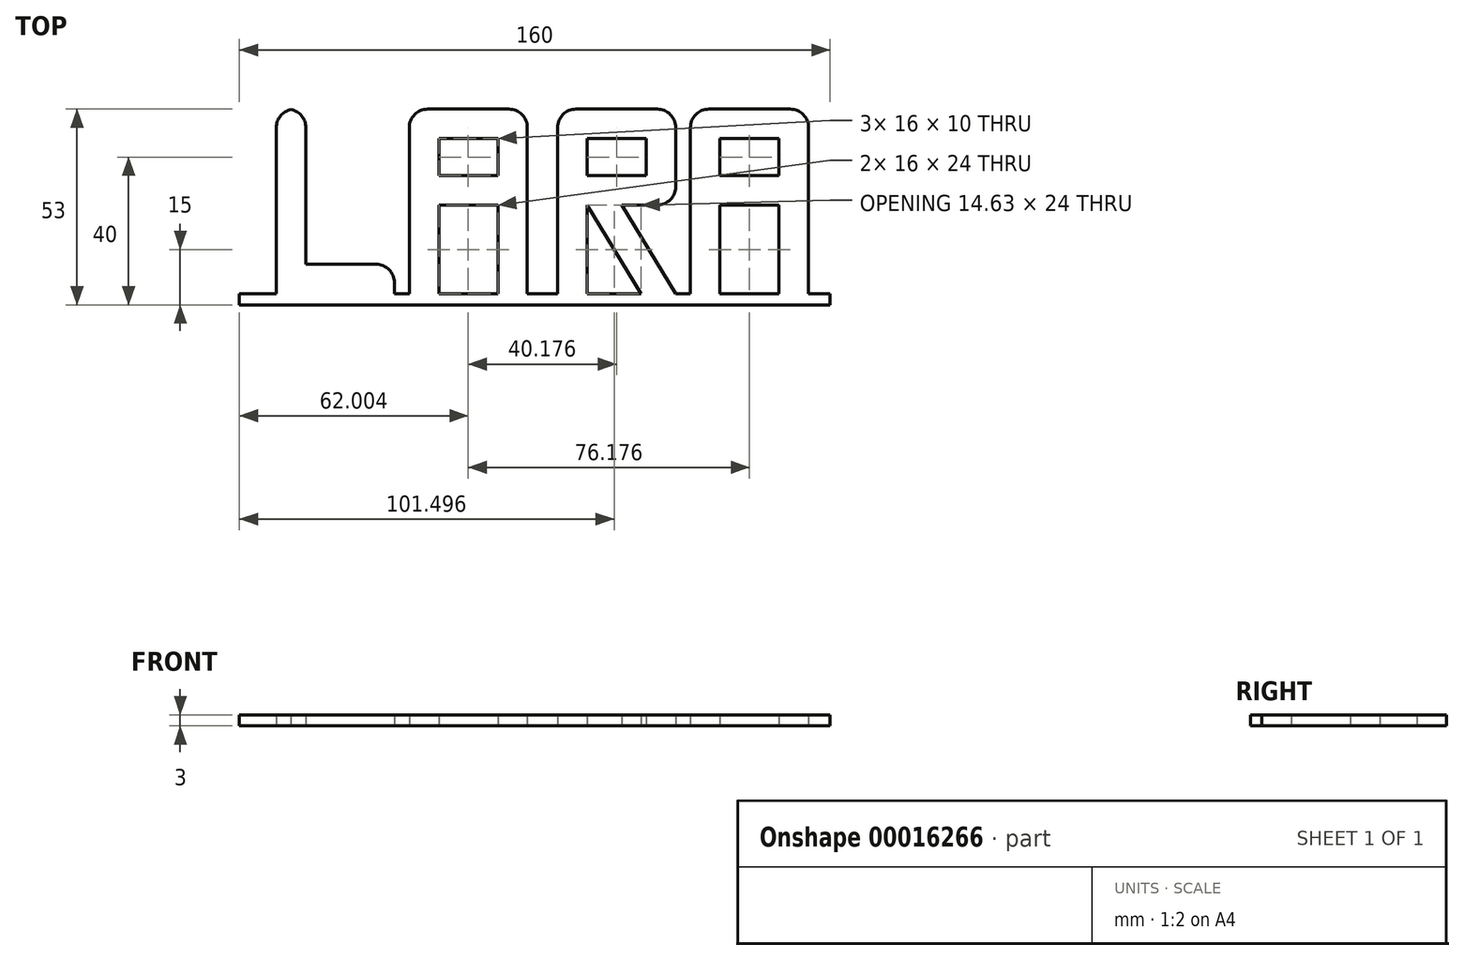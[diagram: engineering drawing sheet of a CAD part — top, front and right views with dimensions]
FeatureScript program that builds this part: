
annotation { "Feature Type Name" : "Feature", "Feature Type Description" : "" }
export const myFeature = defineFeature(function(context is Context, id is Id, definition is map)
    precondition{}
    {
        {
            var Q0;
            Q0=qCreatedBy(makeId("Top.planeOp"),FACE);
            var sketch = newSketch(context, id + "F0", { "sketchPlane" : qUnion([Q0])});
            skLineSegment(sketch, "E0.rect.bottom", {"start": v(71.24, 0) * mm, "end": v(-88.76, 0) * mm});
            skLineSegment(sketch, "E0.rect.top", {"start": v(71.24, 3) * mm, "end": v(-88.76, 3) * mm});
            skLineSegment(sketch, "E0.rect.left", {"start": v(71.24, 0) * mm, "end": v(71.24, 3) * mm});
            skLineSegment(sketch, "E0.rect.right", {"start": v(-88.76, 0) * mm, "end": v(-88.76, 3) * mm});
            skPoint(sketch, "E0.rect.middle", {"position": v(-8.76, 1.5) * mm});
            skSolve(sketch);
        }
        {
            var Q0;
            Q0 = qSketchRegion(id + "F0", true);
            extrude(context, id + "F1", {"entities" : qUnion([Q0]), "depth" : 3 * mm});
        }
        {
            var Q0;
            Q0=qCreatedBy(makeId("Top.planeOp"),FACE);
            var sketch = newSketch(context, id + "F2", { "sketchPlane" : qUnion([Q0])});
            skLineSegment(sketch, "E1.bottom", {"start": v(-78.76, 53) * mm, "end": v(-70.76, 53) * mm});
            skLineSegment(sketch, "E1.top", {"start": v(-78.76, 3) * mm, "end": v(-46.76, 3) * mm});
            skLineSegment(sketch, "E1.left", {"start": v(-78.76, 53) * mm, "end": v(-78.76, 3) * mm});
            skLineSegment(sketch, "E1.right", {"start": v(-46.76, 11) * mm, "end": v(-46.76, 3) * mm});
            skLineSegment(sketch, "E2.top", {"start": v(-46.76, 11) * mm, "end": v(-70.76, 11) * mm});
            skLineSegment(sketch, "E2.right", {"start": v(-70.76, 53) * mm, "end": v(-70.76, 11) * mm});
            skSolve(sketch);
        }
        {
            var Q0;
            Q0=makeQuery(id+"F2.imprint","IMPRINT",FACE,{"disambiguationData":[TD([[makeQuery(id+"F2.imprint","IMPRINT",EDGE,{"derivedFrom":sQuery(id+"F2.wireOp",EDGE,"E1.bottom")}),-1.0]])]});
            extrude(context, id + "F3", {"entities" : qUnion([Q0]), "operationType" : NewBodyOperationType.ADD, "depth" : 3 * mm});
        }
        {
            var Q0;
            Q0=qCreatedBy(makeId("Top.planeOp"),FACE);
            var sketch = newSketch(context, id + "F4", { "sketchPlane" : qUnion([Q0])});
            skLineSegment(sketch, "E3.bottom", {"start": v(-42.76, 3) * mm, "end": v(-10.76, 3) * mm});
            skLineSegment(sketch, "E3.top", {"start": v(-42.76, 53) * mm, "end": v(-10.76, 53) * mm});
            skLineSegment(sketch, "E3.left", {"start": v(-42.76, 3) * mm, "end": v(-42.76, 53) * mm});
            skLineSegment(sketch, "E3.right", {"start": v(-10.76, 3) * mm, "end": v(-10.76, 53) * mm});
            skLineSegment(sketch, "E4.bottom", {"start": v(-34.76, 3) * mm, "end": v(-18.76, 3) * mm});
            skLineSegment(sketch, "E4.top", {"start": v(-34.76, 27) * mm, "end": v(-18.76, 27) * mm});
            skLineSegment(sketch, "E4.left", {"start": v(-34.76, 3) * mm, "end": v(-34.76, 27) * mm});
            skLineSegment(sketch, "E4.right", {"start": v(-18.76, 3) * mm, "end": v(-18.76, 27) * mm});
            skLineSegment(sketch, "E5.bottom", {"start": v(-34.76, 45) * mm, "end": v(-18.76, 45) * mm});
            skLineSegment(sketch, "E5.top", {"start": v(-34.76, 35) * mm, "end": v(-18.76, 35) * mm});
            skLineSegment(sketch, "E5.left", {"start": v(-34.76, 45) * mm, "end": v(-34.76, 35) * mm});
            skLineSegment(sketch, "E5.right", {"start": v(-18.76, 45) * mm, "end": v(-18.76, 35) * mm});
            skSolve(sketch);
        }
        {
            var Q0;
            Q0=makeQuery(id+"F4.imprint","IMPRINT",FACE,{"disambiguationData":[TD([[makeQuery(id+"F4.imprint","IMPRINT",EDGE,{"derivedFrom":sQuery(id+"F4.wireOp",EDGE,"E3.top")}),-1.0]])]});
            extrude(context, id + "F5", {"entities" : qUnion([Q0]), "operationType" : NewBodyOperationType.ADD, "depth" : 3 * mm});
        }
        {
            var Q0;
            Q0=qCreatedBy(makeId("Top.planeOp"),FACE);
            var sketch = newSketch(context, id + "F6", { "sketchPlane" : qUnion([Q0])});
            skLineSegment(sketch, "E6.bottom", {"start": v(-2.58, 53) * mm, "end": v(29.42, 53) * mm});
            skLineSegment(sketch, "E6.top", {"start": v(-2.58, 3) * mm, "end": v(29.42, 3) * mm});
            skLineSegment(sketch, "E6.left", {"start": v(-2.58, 53) * mm, "end": v(-2.58, 3) * mm});
            skLineSegment(sketch, "E6.right", {"start": v(29.42, 53) * mm, "end": v(29.42, 3) * mm});
            skLineSegment(sketch, "E7.bottom", {"start": v(5.42, 45) * mm, "end": v(21.42, 45) * mm});
            skLineSegment(sketch, "E7.top", {"start": v(5.42, 35) * mm, "end": v(21.42, 35) * mm});
            skLineSegment(sketch, "E7.left", {"start": v(5.42, 45) * mm, "end": v(5.42, 35) * mm});
            skLineSegment(sketch, "E7.right", {"start": v(21.42, 45) * mm, "end": v(21.42, 35) * mm});
            skLineSegment(sketch, "E8", {"start": v(5.42, 27) * mm, "end": v(5.42, 3) * mm});
            skLineSegment(sketch, "E9", {"start": v(29.42, 3) * mm, "end": v(14.8, 27) * mm});
            skLineSegment(sketch, "E10", {"start": v(14.8, 27) * mm, "end": v(29.42, 27) * mm});
            skLineSegment(sketch, "E11", {"start": v(5.42, 27) * mm, "end": v(20.05, 3) * mm});
            skSolve(sketch);
        }
        {
            var Q0;
            {var subQ5=sQuery(id+"F6.wireOp",EDGE,"E6.bottom");Q0=makeQuery(id+"F6.imprint","IMPRINT",FACE,{"disambiguationData":[TD([[makeQuery(id+"F6.imprint","IMPRINT",EDGE,{"derivedFrom":subQ5}),-1.0]])]});}
            extrude(context, id + "F7", {"entities" : qUnion([Q0]), "operationType" : NewBodyOperationType.ADD, "depth" : 3 * mm});
        }
        {
            var Q0;
            Q0=makeQuery(id+"F3.opExtrude","SWEPT_EDGE",EDGE,{"disambiguationData":[OSD([sQuery(id+"F2.wireOp",EDGE,"E1.bottom"),sQuery(id+"F2.wireOp",EDGE,"E1.left")])]});
            var Q1;
            Q1=makeQuery(id+"F3.opExtrude","SWEPT_EDGE",EDGE,{"disambiguationData":[OSD([sQuery(id+"F2.wireOp",EDGE,"E1.bottom"),sQuery(id+"F2.wireOp",EDGE,"E2.right")])]});
            var Q2;
            Q2=makeQuery(id+"F5.opExtrude","SWEPT_EDGE",EDGE,{"disambiguationData":[OSD([sQuery(id+"F4.wireOp",EDGE,"E3.top"),sQuery(id+"F4.wireOp",EDGE,"E3.left")])]});
            var Q3;
            Q3=makeQuery(id+"F5.opExtrude","SWEPT_EDGE",EDGE,{"disambiguationData":[OSD([sQuery(id+"F4.wireOp",EDGE,"E3.top"),sQuery(id+"F4.wireOp",EDGE,"E3.right")])]});
            var Q4;
            Q4=makeQuery(id+"F7.opExtrude","SWEPT_EDGE",EDGE,{"disambiguationData":[OSD([sQuery(id+"F6.wireOp",EDGE,"E6.bottom"),sQuery(id+"F6.wireOp",EDGE,"E6.left")])]});
            var Q5;
            Q5=makeQuery(id+"F7.opExtrude","SWEPT_EDGE",EDGE,{"disambiguationData":[OSD([sQuery(id+"F6.wireOp",EDGE,"E6.bottom"),sQuery(id+"F6.wireOp",EDGE,"E6.right")])]});
            var Q6;
            Q6=makeQuery(id+"F3.opExtrude","SWEPT_EDGE",EDGE,{"disambiguationData":[OSD([sQuery(id+"F2.wireOp",EDGE,"E1.right"),sQuery(id+"F2.wireOp",EDGE,"E2.top")])]});
            var Q7;
            Q7=makeQuery(id+"F7.opExtrude","SWEPT_EDGE",EDGE,{"disambiguationData":[OSD([sQuery(id+"F6.wireOp",EDGE,"E6.right"),sQuery(id+"F6.wireOp",EDGE,"E10")])]});
            fillet(context, id + "F8", {"entities" : qUnion([Q0, Q1, Q2, Q3, Q4, Q5, Q6, Q7]), "radius" : 5 * mm, "tangentPropagation" : true, "allowEdgeOverflow" : false});
        }
        {
            var Q0;
            Q0=qCreatedBy(makeId("Top.planeOp"),FACE);
            var sketch = newSketch(context, id + "F9", { "sketchPlane" : qUnion([Q0])});
            skLineSegment(sketch, "E12.bottom", {"start": v(33.42, 3) * mm, "end": v(65.42, 3) * mm});
            skLineSegment(sketch, "E12.top", {"start": v(33.42, 53) * mm, "end": v(65.42, 53) * mm});
            skLineSegment(sketch, "E12.left", {"start": v(33.42, 3) * mm, "end": v(33.42, 53) * mm});
            skLineSegment(sketch, "E12.right", {"start": v(65.42, 3) * mm, "end": v(65.42, 53) * mm});
            skLineSegment(sketch, "E13.bottom", {"start": v(41.42, 45) * mm, "end": v(57.42, 45) * mm});
            skLineSegment(sketch, "E13.top", {"start": v(41.42, 35) * mm, "end": v(57.42, 35) * mm});
            skLineSegment(sketch, "E13.left", {"start": v(41.42, 45) * mm, "end": v(41.42, 35) * mm});
            skLineSegment(sketch, "E13.right", {"start": v(57.42, 45) * mm, "end": v(57.42, 35) * mm});
            skLineSegment(sketch, "E14.bottom", {"start": v(41.42, 3) * mm, "end": v(57.42, 3) * mm});
            skLineSegment(sketch, "E14.top", {"start": v(41.42, 27) * mm, "end": v(57.42, 27) * mm});
            skLineSegment(sketch, "E14.left", {"start": v(41.42, 3) * mm, "end": v(41.42, 27) * mm});
            skLineSegment(sketch, "E14.right", {"start": v(57.42, 3) * mm, "end": v(57.42, 27) * mm});
            skSolve(sketch);
        }
        {
            var Q0;
            Q0=makeQuery(id+"F9.imprint","IMPRINT",FACE,{"disambiguationData":[TD([[makeQuery(id+"F9.imprint","IMPRINT",EDGE,{"derivedFrom":sQuery(id+"F9.wireOp",EDGE,"E12.top")}),-1.0]])]});
            extrude(context, id + "F10", {"entities" : qUnion([Q0]), "operationType" : NewBodyOperationType.ADD, "depth" : 3 * mm});
        }
        {
            var Q0;
            Q0=makeQuery(id+"F10.opExtrude","SWEPT_EDGE",EDGE,{"disambiguationData":[OSD([sQuery(id+"F9.wireOp",EDGE,"E12.top"),sQuery(id+"F9.wireOp",EDGE,"E12.right")])]});
            var Q1;
            Q1=makeQuery(id+"F10.opExtrude","SWEPT_EDGE",EDGE,{"disambiguationData":[OSD([sQuery(id+"F9.wireOp",EDGE,"E12.top"),sQuery(id+"F9.wireOp",EDGE,"E12.left")])]});
            fillet(context, id + "F11", {"entities" : qUnion([Q0, Q1]), "radius" : 5 * mm, "tangentPropagation" : true, "allowEdgeOverflow" : false});
        }
    });
